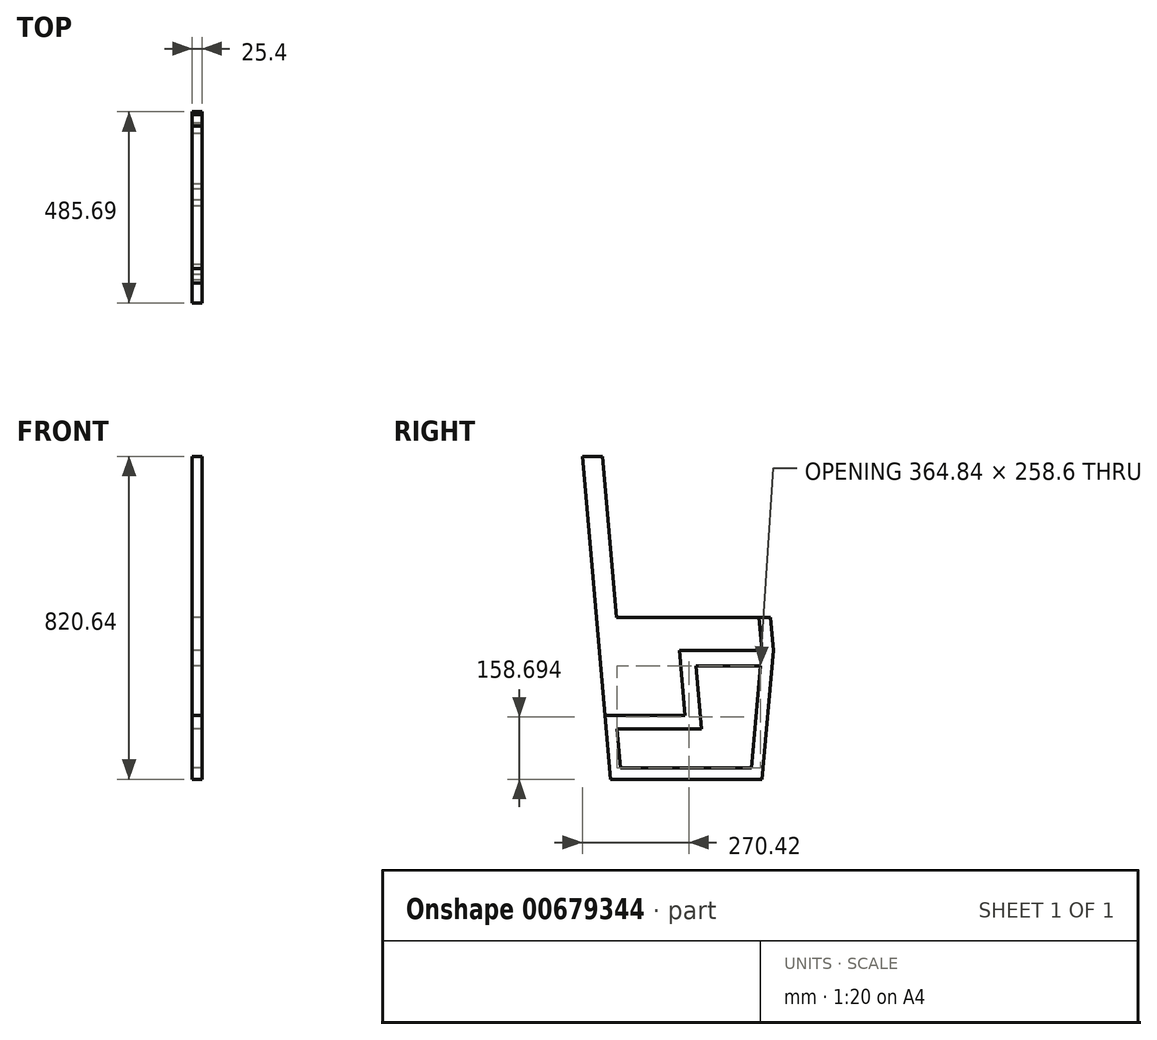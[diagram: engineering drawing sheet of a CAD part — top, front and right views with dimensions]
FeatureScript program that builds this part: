
annotation { "Feature Type Name" : "Feature", "Feature Type Description" : "" }
export const myFeature = defineFeature(function(context is Context, id is Id, definition is map)
    precondition{}
    {
        {
            var Q0;
            Q0=qCreatedBy(makeId("Right.planeOp"),FACE);
            var sketch = newSketch(context, id + "F0", { "sketchPlane" : qUnion([Q0])});
            skLineSegment(sketch, "E0", {"start": v(14.83, -1.72) * mm, "end": v(0.44, 162.75) * mm});
            skLineSegment(sketch, "E1", {"start": v(203.64, 162.75) * mm, "end": v(0.44, 162.75) * mm});
            skLineSegment(sketch, "E2", {"start": v(203.64, 162.75) * mm, "end": v(189.25, 327.22) * mm});
            skLineSegment(sketch, "E3", {"start": v(612.73, 411.18) * mm, "end": v(612.73, 0) * mm, "construction": true});
            skLineSegment(sketch, "E4", {"start": v(0, 162.12) * mm, "end": v(-965.57, 162.12) * mm, "construction": true});
            skLineSegment(sketch, "E5", {"start": v(406.4, 0) * mm, "end": v(0, 0) * mm});
            skLineSegment(sketch, "E6", {"start": v(612.73, 0) * mm, "end": v(406.4, 0) * mm, "construction": true});
            skLineSegment(sketch, "E7", {"start": v(421.23, 411.18) * mm, "end": v(29.5, 411.18) * mm});
            skLineSegment(sketch, "E8", {"start": v(-21.15, 409.46) * mm, "end": v(0.44, 162.75) * mm});
            skLineSegment(sketch, "E9", {"start": v(421.23, 411.18) * mm, "end": v(612.73, 411.18) * mm, "construction": true});
            skLineSegment(sketch, "E10", {"start": v(-21.15, 409.46) * mm, "end": v(-57.12, 820.64) * mm});
            skLineSegment(sketch, "E11", {"start": v(-40.5, 162.12) * mm, "end": v(0, 162.12) * mm});
            skLineSegment(sketch, "E12", {"start": v(406.4, 0) * mm, "end": v(457.2, 0) * mm});
            skLineSegment(sketch, "E13", {"start": v(-6.32, 820.64) * mm, "end": v(29.5, 411.18) * mm});
            skLineSegment(sketch, "E14", {"start": v(421.23, 411.18) * mm, "end": v(457.2, 0) * mm});
            skLineSegment(sketch, "E15.top", {"start": v(231.26, 288) * mm, "end": v(395.72, 288) * mm});
            skLineSegment(sketch, "E15.left", {"start": v(256.86, -4.71) * mm, "end": v(231.26, 288) * mm});
            skLineSegment(sketch, "E16.bottom", {"start": v(42.11, 0) * mm, "end": v(216.94, 0) * mm});
            skLineSegment(sketch, "E16.top", {"start": v(30.88, 128.38) * mm, "end": v(205.7, 128.38) * mm});
            skLineSegment(sketch, "E16.left", {"start": v(42.11, 0) * mm, "end": v(30.88, 128.38) * mm});
            skLineSegment(sketch, "E17", {"start": v(399.15, 327.22) * mm, "end": v(391.55, 414.15) * mm});
            skLineSegment(sketch, "E18", {"start": v(-57.12, 820.64) * mm, "end": v(-6.32, 820.64) * mm});
            skLineSegment(sketch, "E19", {"start": v(399.15, 327.22) * mm, "end": v(428.57, 327.23) * mm});
            skLineSegment(sketch, "E20", {"start": v(428.57, 327.23) * mm, "end": v(390.24, -110.9) * mm});
            skLineSegment(sketch, "E21", {"start": v(399.15, 327.22) * mm, "end": v(364.45, -69.37) * mm});
            skLineSegment(sketch, "E22", {"start": v(205.7, 128.38) * mm, "end": v(245.22, 128.38) * mm});
            skLineSegment(sketch, "E23", {"start": v(48.15, 200.7) * mm, "end": v(-2.88, 200.7) * mm});
            skLineSegment(sketch, "E24", {"start": v(39.54, 29.4) * mm, "end": v(373.1, 29.4) * mm});
            skLineSegment(sketch, "E25", {"start": v(189.25, 327.22) * mm, "end": v(399.15, 327.22) * mm});
            skSolve(sketch);
        }
        {
            var Q0;
            {var subQ0=sQuery(id+"F0.wireOp",EDGE,"E10");Q0=makeQuery(id+"F0.imprint","IMPRINT",FACE,{"disambiguationData":[TD([[makeQuery(id+"F0.imprint","IMPRINT",EDGE,{"derivedFrom":subQ0}),-1.0]])]});}
            var Q1;
            Q1=makeQuery(id+"F0.imprint","IMPRINT",FACE,{"disambiguationData":[TD([[makeQuery(id+"F0.imprint","IMPRINT",EDGE,{"derivedFrom":sQuery(id+"F0.wireOp",EDGE,"E1")}),-1.0]])]});
            var Q2;
            {var subQ0=sQuery(id+"F0.wireOp",EDGE,"E17");var subQ5=sQuery(id+"F0.wireOp",EDGE,"E7");var subQ6=makeQuery(id+"F0.imprint","INTERSECT",VERTEX,{"derivedFrom":[subQ5,subQ0]});Q2=makeQuery(id+"F0.imprint","IMPRINT",FACE,{"disambiguationData":[TD([[makeQuery(id+"F0.imprint","IMPRINT",EDGE,{"disambiguationData":[TD([[subQ6,-1.0]])],"derivedFrom":subQ5}),1.0]])]});}
            var Q3;
            {var subQ0=sQuery(id+"F0.wireOp",EDGE,"oCBdQ26A-LFMd-S9sW-sYZx-xYRC6UpzZG1i.top");Q3=makeQuery(id+"F0.imprint","IMPRINT",FACE,{"disambiguationData":[TD([[makeQuery(id+"F0.imprint","IMPRINT",EDGE,{"derivedFrom":subQ0}),1.0]])]});}
            extrude(context, id + "F1", {"entities" : qUnion([Q0, Q1, Q2, Q3]), "depth" : 25.4 * mm, "offsetDistance" : 25.4 * mm});
        }
        {
            var Q0;
            Q0=makeQuery(id+"F0.imprint","IMPRINT",FACE,{"disambiguationData":[TD([[makeQuery(id+"F0.imprint","IMPRINT",EDGE,{"derivedFrom":sQuery(id+"F0.wireOp",EDGE,"oAci7Kaw-5Hkm-9jKa-Rgxa-tkB4P00vJvvU")}),1.0]])]});
            var Q1;
            Q1=makeQuery(id+"F0.imprint","IMPRINT",FACE,{"disambiguationData":[TD([[makeQuery(id+"F0.imprint","IMPRINT",EDGE,{"derivedFrom":sQuery(id+"F0.wireOp",EDGE,"E0")}),-1.0]])]});
            var Q2;
            {var subQ0=sQuery(id+"F0.wireOp",EDGE,"E15.top");var subQ1=sQuery(id+"F0.wireOp",EDGE,"oAci7Kaw-5Hkm-9jKa-Rgxa-tkB4P00vJvvU");var subQ2=makeQuery(id+"F0.imprint","INTERSECT",VERTEX,{"derivedFrom":[subQ1,subQ0]});Q2=makeQuery(id+"F0.imprint","IMPRINT",FACE,{"disambiguationData":[TD([[makeQuery(id+"F0.imprint","IMPRINT",EDGE,{"disambiguationData":[TD([[subQ2,-1.0]])],"derivedFrom":subQ1}),-1.0]])]});}
            var Q3;
            {var subQ0=sQuery(id+"F0.wireOp",EDGE,"oAci7Kaw-5Hkm-9jKa-Rgxa-tkB4P00vJvvU");var subQ5=sQuery(id+"F0.wireOp",EDGE,"E15.top");var subQ7=makeQuery(id+"F0.imprint","INTERSECT",VERTEX,{"derivedFrom":[subQ0,subQ5]});Q3=makeQuery(id+"F0.imprint","IMPRINT",FACE,{"disambiguationData":[TD([[makeQuery(id+"F0.imprint","IMPRINT",EDGE,{"disambiguationData":[TD([[subQ7,1.0]])],"derivedFrom":subQ5}),1.0]])]});}
            var Q4;
            {var subQ1=sQuery(id+"F0.wireOp",EDGE,"E7");var subQ3=sQuery(id+"F0.wireOp",EDGE,"E17");var subQ4=makeQuery(id+"F0.imprint","INTERSECT",VERTEX,{"derivedFrom":[subQ1,subQ3]});Q4=makeQuery(id+"F0.imprint","IMPRINT",FACE,{"disambiguationData":[TD([[makeQuery(id+"F0.imprint","IMPRINT",EDGE,{"disambiguationData":[TD([[subQ4,1.0]])],"derivedFrom":subQ1}),1.0]])]});}
            var Q5;
            {var subQ1=sQuery(id+"F0.wireOp",EDGE,"E14");var subQ3=sQuery(id+"F0.wireOp",EDGE,"E19");var subQ4=makeQuery(id+"F0.imprint","INTERSECT",VERTEX,{"derivedFrom":[subQ1,subQ3]});Q5=makeQuery(id+"F0.imprint","IMPRINT",FACE,{"disambiguationData":[TD([[makeQuery(id+"F0.imprint","IMPRINT",EDGE,{"disambiguationData":[TD([[subQ4,1.0]])],"derivedFrom":subQ3}),1.0]])]});}
            var Q6;
            {var subQ1=sQuery(id+"F0.wireOp",EDGE,"E19");Q6=makeQuery(id+"F0.imprint","IMPRINT",FACE,{"disambiguationData":[TD([[makeQuery(id+"F0.imprint","IMPRINT",EDGE,{"derivedFrom":subQ1}),-1.0]])]});}
            var Q7;
            {var subQ0=sQuery(id+"F0.wireOp",EDGE,"E16.bottom");Q7=makeQuery(id+"F0.imprint","IMPRINT",FACE,{"disambiguationData":[TD([[makeQuery(id+"F0.imprint","IMPRINT",EDGE,{"derivedFrom":subQ0}),1.0]])]});}
            var Q8;
            {var subQ1=sQuery(id+"F0.wireOp",EDGE,"E5");var subQ3=sQuery(id+"F0.wireOp",EDGE,"E15.left");var subQ4=makeQuery(id+"F0.imprint","INTERSECT",VERTEX,{"derivedFrom":[subQ1,subQ3]});Q8=makeQuery(id+"F0.imprint","IMPRINT",FACE,{"disambiguationData":[TD([[makeQuery(id+"F0.imprint","IMPRINT",EDGE,{"disambiguationData":[TD([[subQ4,-1.0]])],"derivedFrom":subQ3}),1.0]])]});}
            var Q9;
            {var subQ0=sQuery(id+"F0.wireOp",EDGE,"E21");var subQ1=sQuery(id+"F0.wireOp",EDGE,"E5");var subQ2=makeQuery(id+"F0.imprint","INTERSECT",VERTEX,{"derivedFrom":[subQ1,subQ0]});Q9=makeQuery(id+"F0.imprint","IMPRINT",FACE,{"disambiguationData":[TD([[makeQuery(id+"F0.imprint","IMPRINT",EDGE,{"disambiguationData":[TD([[subQ2,-1.0]])],"derivedFrom":subQ1}),-1.0]])]});}
            extrude(context, id + "F2", {"entities" : qUnion([Q0, Q1, Q2, Q3, Q4, Q5, Q6, Q7, Q8, Q9]), "depth" : 25.4 * mm, "offsetDistance" : 25.4 * mm});
        }
    });
